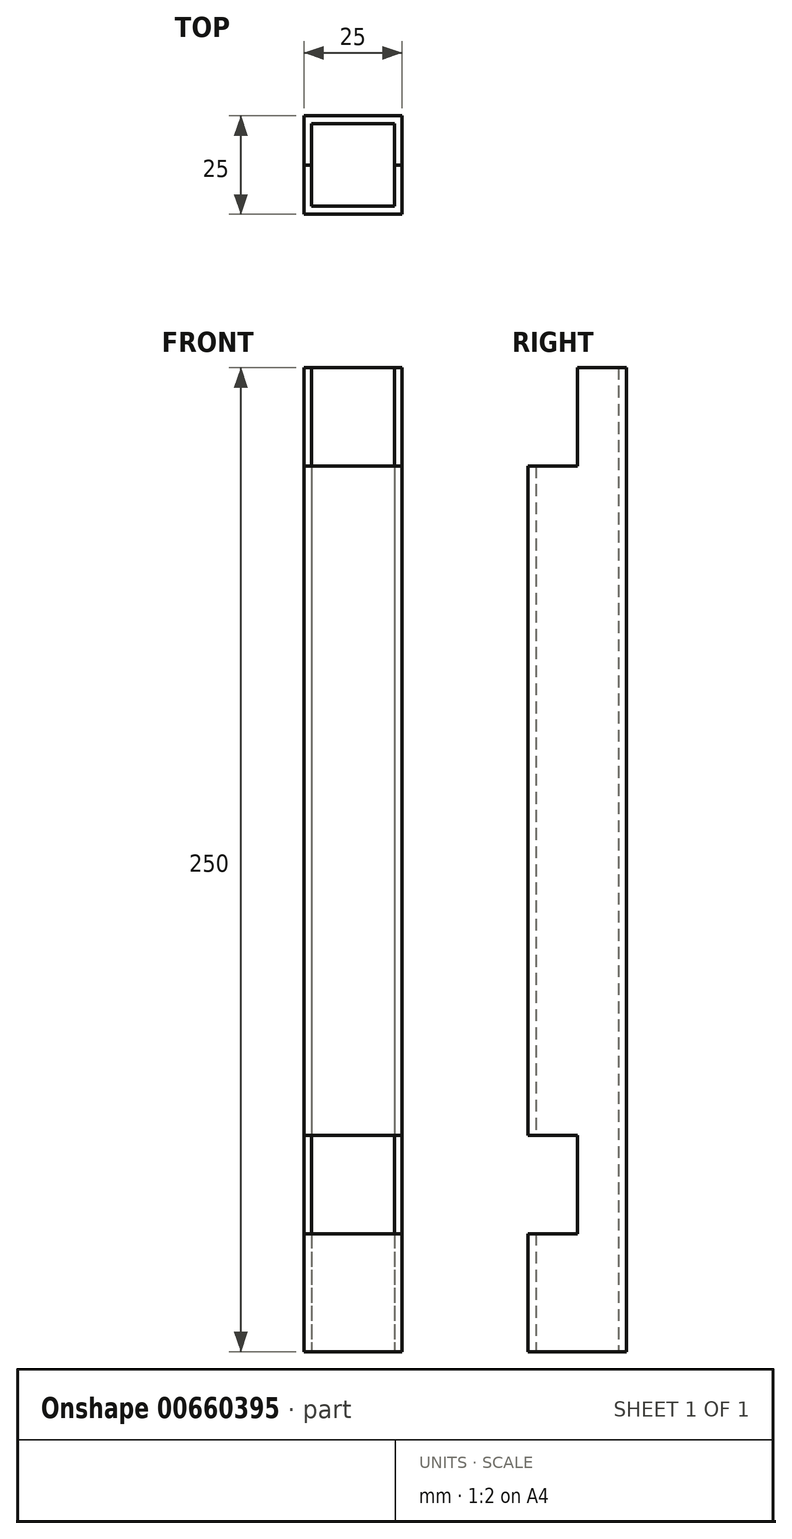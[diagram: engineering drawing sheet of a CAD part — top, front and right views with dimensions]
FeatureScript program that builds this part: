
annotation { "Feature Type Name" : "Feature", "Feature Type Description" : "" }
export const myFeature = defineFeature(function(context is Context, id is Id, definition is map)
    precondition{}
    {
        {
            var Q0;
            Q0=qCreatedBy(makeId("Top.planeOp"),FACE);
            var sketch = newSketch(context, id + "F0", { "sketchPlane" : qUnion([Q0])});
            skLineSegment(sketch, "E0.bottom", {"start": v(0, 0) * mm, "end": v(25, 0) * mm});
            skLineSegment(sketch, "E0.top", {"start": v(0, 25) * mm, "end": v(25, 25) * mm});
            skLineSegment(sketch, "E0.left", {"start": v(0, 0) * mm, "end": v(0, 25) * mm});
            skLineSegment(sketch, "E0.right", {"start": v(25, 0) * mm, "end": v(25, 25) * mm});
            skLineSegment(sketch, "E1.0", {"start": v(2, 23) * mm, "end": v(23, 23) * mm});
            skLineSegment(sketch, "E1.1", {"start": v(2, 2) * mm, "end": v(2, 23) * mm});
            skLineSegment(sketch, "E1.2", {"start": v(2, 2) * mm, "end": v(23, 2) * mm});
            skLineSegment(sketch, "E1.3", {"start": v(23, 2) * mm, "end": v(23, 23) * mm});
            skSolve(sketch);
        }
        {
            var Q0;
            Q0=makeQuery(id+"F0.imprint","IMPRINT",FACE,{"disambiguationData":[TD([[makeQuery(id+"F0.imprint","IMPRINT",EDGE,{"derivedFrom":sQuery(id+"F0.wireOp",EDGE,"E0.bottom")}),1.0]])]});
            extrude(context, id + "F1", {"entities" : qUnion([Q0]), "depth" : 250 * mm, "offsetDistance" : 25 * mm});
        }
        {
            var Q0;
            Q0=makeQuery(id+"F1.opExtrude","SWEPT_FACE",FACE,{"disambiguationData":[OSD([sQuery(id+"F0.wireOp",EDGE,"E0.right")])]});
            var sketch = newSketch(context, id + "F2", { "sketchPlane" : qUnion([Q0])});
            skLineSegment(sketch, "E2.bottom", {"start": v(0, 250) * mm, "end": v(12.5, 250) * mm});
            skLineSegment(sketch, "E2.top", {"start": v(0, 225) * mm, "end": v(12.5, 225) * mm});
            skLineSegment(sketch, "E2.left", {"start": v(0, 250) * mm, "end": v(0, 225) * mm});
            skLineSegment(sketch, "E2.right", {"start": v(12.5, 250) * mm, "end": v(12.5, 225) * mm});
            skLineSegment(sketch, "E3.bottom", {"start": v(0, 55) * mm, "end": v(12.5, 55) * mm});
            skLineSegment(sketch, "E3.top", {"start": v(0, 30) * mm, "end": v(12.5, 30) * mm});
            skLineSegment(sketch, "E3.left", {"start": v(0, 55) * mm, "end": v(0, 30) * mm});
            skLineSegment(sketch, "E3.right", {"start": v(12.5, 55) * mm, "end": v(12.5, 30) * mm});
            skSolve(sketch);
        }
        {
            var Q0;
            Q0=makeQuery(id+"F2.imprint","IMPRINT",FACE,{"disambiguationData":[TD([[makeQuery(id+"F2.imprint","IMPRINT",EDGE,{"derivedFrom":sQuery(id+"F2.wireOp",EDGE,"E2.bottom")}),-1.0]])]});
            var Q1;
            Q1=makeQuery(id+"F2.imprint","IMPRINT",FACE,{"disambiguationData":[TD([[makeQuery(id+"F2.imprint","IMPRINT",EDGE,{"derivedFrom":sQuery(id+"F2.wireOp",EDGE,"E3.bottom")}),-1.0]])]});
            extrude(context, id + "F3", {"entities" : qUnion([Q0, Q1]), "operationType" : NewBodyOperationType.REMOVE, "endBound" : BoundingType.THROUGH_ALL, "oppositeDirection" : true, "depth" : 25 * mm, "offsetDistance" : 25 * mm});
        }
    });
